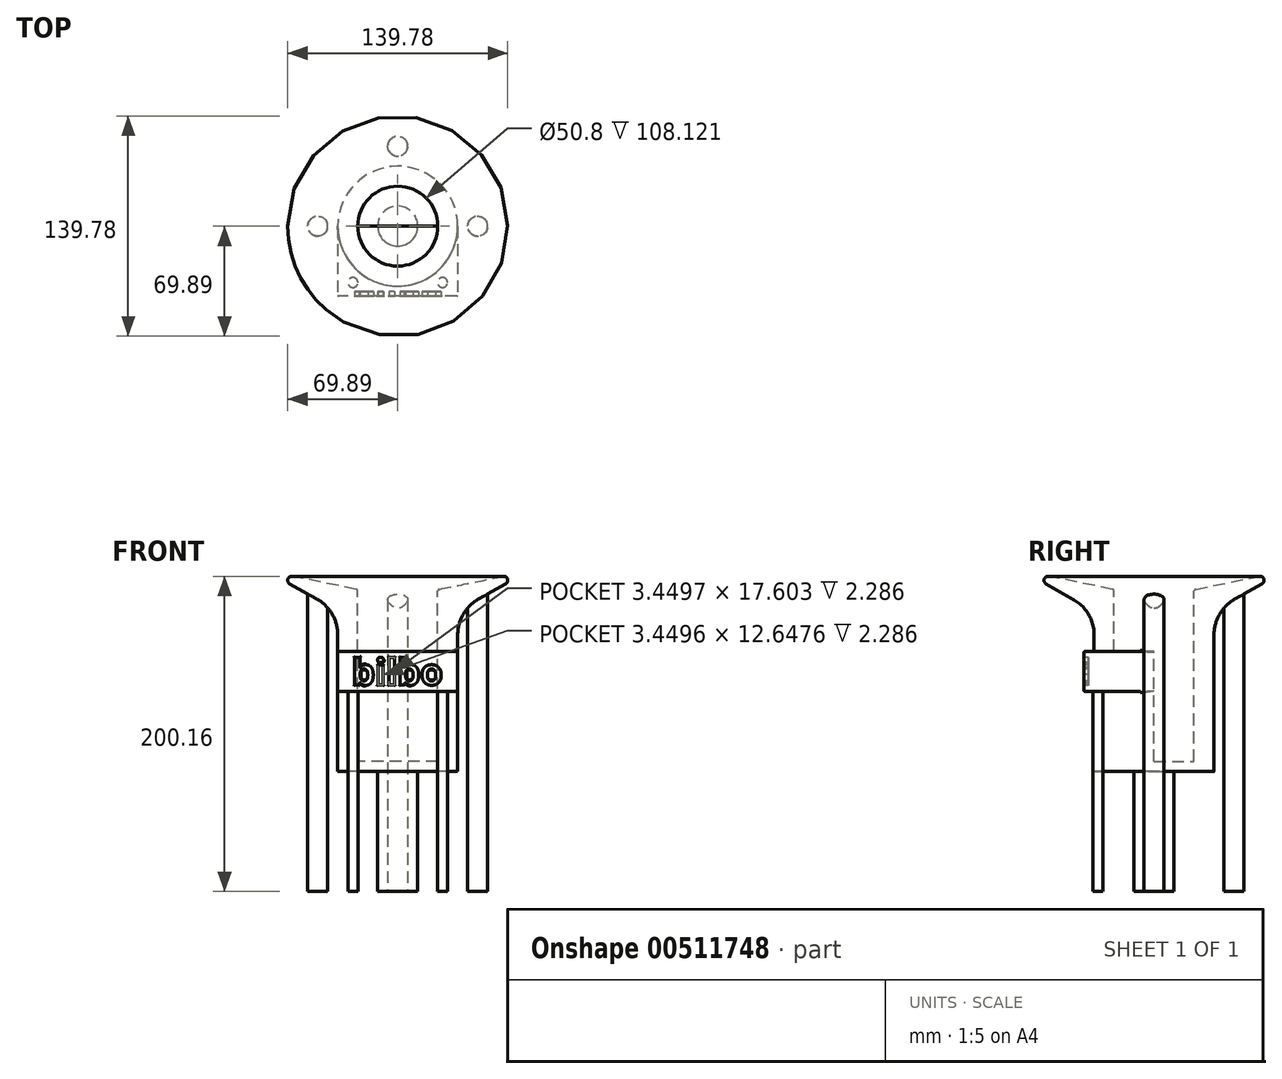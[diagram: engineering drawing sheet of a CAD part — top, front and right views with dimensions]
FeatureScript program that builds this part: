
annotation { "Feature Type Name" : "Feature", "Feature Type Description" : "" }
export const myFeature = defineFeature(function(context is Context, id is Id, definition is map)
    precondition{}
    {
        {
            var Q0;
            Q0=qCreatedBy(makeId("Front.planeOp"),FACE);
            var sketch = newSketch(context, id + "F0", { "sketchPlane" : qUnion([Q0])});
            skLineSegment(sketch, "E0", {"start": v(0, 0) * mm, "end": v(0, -6.35) * mm});
            skLineSegment(sketch, "E1", {"start": v(0, -6.35) * mm, "end": v(38.1, -6.35) * mm});
            skLineSegment(sketch, "E2", {"start": v(38.1, -6.35) * mm, "end": v(38.1, 95.25) * mm});
            skLineSegment(sketch, "E3", {"start": v(38.1, 95.25) * mm, "end": v(82.1, 120.65) * mm});
            skLineSegment(sketch, "E4", {"start": v(0, 0) * mm, "end": v(25.4, 0) * mm});
            skLineSegment(sketch, "E5", {"start": v(25.4, 0) * mm, "end": v(25.4, 109.16) * mm});
            skLineSegment(sketch, "E6", {"start": v(82.1, 120.65) * mm, "end": v(25.4, 109.16) * mm});
            skSolve(sketch);
        }
        {
            var Q0;
            Q0=makeQuery(id+"F0.imprint","IMPRINT",FACE,{"disambiguationData":[TD([[makeQuery(id+"F0.imprint","IMPRINT",EDGE,{"derivedFrom":sQuery(id+"F0.wireOp",EDGE,"E0")}),1.0]])]});
            var Q1;
            Q1=sQuery(id+"F0.wireOp",EDGE,"E0");
            revolve(context, id + "F1", {"entities" : qUnion([Q0]), "axis" : qUnion([Q1]), "revolveType" : RevolveType.FULL});
        }
        {
            var Q0;
            Q0=makeQuery(id+"F1.opRevolve","SWEPT_EDGE",EDGE,{"disambiguationData":[OSD([sQuery(id+"F0.wireOp",EDGE,"E3"),sQuery(id+"F0.wireOp",EDGE,"E6")])]});
            fillet(context, id + "F2", {"entities" : qUnion([Q0]), "radius" : 2.54 * mm, "tangentPropagation" : true, "allowEdgeOverflow" : false});
        }
        {
            var Q0;
            Q0=makeQuery(id+"F1.opRevolve","SWEPT_EDGE",EDGE,{"disambiguationData":[OSD([sQuery(id+"F0.wireOp",EDGE,"E5"),sQuery(id+"F0.wireOp",EDGE,"E6")])]});
            fillet(context, id + "F3", {"entities" : qUnion([Q0]), "radius" : 1.27 * mm, "tangentPropagation" : true, "allowEdgeOverflow" : false});
        }
        {
            var Q0;
            Q0=makeQuery(id+"F1.opRevolve","SWEPT_EDGE",EDGE,{"disambiguationData":[OSD([sQuery(id+"F0.wireOp",EDGE,"E2"),sQuery(id+"F0.wireOp",EDGE,"E3")])]});
            fillet(context, id + "F4", {"entities" : qUnion([Q0]), "radius" : 25.4 * mm, "tangentPropagation" : true, "allowEdgeOverflow" : false});
        }
        {
            var Q0;
            Q0=makeQuery(id+"F1.opRevolve","SWEPT_EDGE",EDGE,{"disambiguationData":[OSD([sQuery(id+"F0.wireOp",EDGE,"E1"),sQuery(id+"F0.wireOp",EDGE,"E2")])]});
            fillet(context, id + "F5", {"entities" : qUnion([Q0]), "radius" : 0.13 * mm, "tangentPropagation" : true, "allowEdgeOverflow" : false});
        }
        {
            var Q0;
            Q0=makeQuery(id+"F1.opRevolve","SWEPT_FACE",FACE,{"disambiguationData":[OSD([sQuery(id+"F0.wireOp",EDGE,"E1")])]});
            var sketch = newSketch(context, id + "F6", { "sketchPlane" : qUnion([Q0])});
            skLineSegment(sketch, "E7", {"start": v(0, 0) * mm, "end": v(-38.1, 0) * mm});
            skLineSegment(sketch, "E8", {"start": v(-38.1, 0) * mm, "end": v(38.1, 0) * mm});
            skLineSegment(sketch, "E9", {"start": v(0, 44.45) * mm, "end": v(-38.1, 44.45) * mm});
            skLineSegment(sketch, "E10", {"start": v(-38.1, 44.45) * mm, "end": v(38.1, 44.45) * mm});
            skLineSegment(sketch, "E11", {"start": v(38.1, 44.45) * mm, "end": v(38.1, 0) * mm});
            skLineSegment(sketch, "E12", {"start": v(-38.1, 44.45) * mm, "end": v(-38.1, 0) * mm});
            skSolve(sketch);
        }
        {
            var Q0;
            Q0 = qSketchRegion(id + "F6", true);
            extrude(context, id + "F7", {"entities" : qUnion([Q0]), "operationType" : NewBodyOperationType.ADD, "depth" : -76.2 * mm});
        }
        {
            var Q0;
            Q0=makeQuery(id+"F7.boolean.opBoolean","MERGE",FACE,{"derivedFrom":[makeQuery(id+"F1.opRevolve","SWEPT_FACE",FACE,{"disambiguationData":[OSD([sQuery(id+"F0.wireOp",EDGE,"E1")])]}),makeQuery(id+"F7.opExtrude","CAP_FACE",FACE,{"disambiguationData":[OSD([sQuery(id+"F6.wireOp",EDGE,"E8"),sQuery(id+"F6.wireOp",EDGE,"E10"),sQuery(id+"F6.wireOp",EDGE,"E11"),sQuery(id+"F6.wireOp",EDGE,"E12")])],"isStart":true})]});
            var sketch = newSketch(context, id + "F8", { "sketchPlane" : qUnion([Q0])});
            skCircle(sketch, "E13", {"center": v(0, 0) * mm, "radius": 38.1 * mm});
            skCircle(sketch, "E14", {"center": v(0, 0) * mm, "radius": 62.93 * mm});
            skSolve(sketch);
        }
        {
            var Q0;
            Q0=makeQuery(id+"F8.imprint","IMPRINT",FACE,{"disambiguationData":[TD([[makeQuery(id+"F8.imprint","IMPRINT",EDGE,{"derivedFrom":sQuery(id+"F8.wireOp",EDGE,"E14")}),1.0]])]});
            var Q1;
            {var subQ3=sQuery(id+"F6.wireOp",EDGE,"E10");Q1=makeQuery(id+"F8.imprint","IMPRINT",FACE,{"disambiguationData":[TD([[makeQuery(id+"F8.imprint","IMPRINT",EDGE,{"derivedFrom":makeQuery(id+"F7.opExtrude","CAP_EDGE",EDGE,{"disambiguationData":[OSD([subQ3])],"isStart":true})}),-1.0]])]});}
            extrude(context, id + "F9", {"entities" : qUnion([Q0, Q1]), "operationType" : NewBodyOperationType.REMOVE, "oppositeDirection" : true, "depth" : 50.8 * mm});
        }
        {
            var Q0;
            Q0=makeQuery(id+"F7.opExtrude","SWEPT_FACE",FACE,{"disambiguationData":[OSD([sQuery(id+"F6.wireOp",EDGE,"E10")])]});
            var sketch = newSketch(context, id + "F10", { "sketchPlane" : qUnion([Q0])});
            skText(sketch, "E15", { "text": "bilbo\n", "fontName": "OpenSans-Bold.ttf"});
            skLineSegment(sketch, "E16.left", {"start": v(63.5, 69.85) * mm, "end": v(63.5, 44.45) * mm});
            skPoint(sketch, "E16.middle", {"position": v(0, 57.15) * mm});
            const initialGuessF10  = {"E15": [-0.0291, 0.04858, 1, 0, 0.01668]};
            skSetInitialGuess(sketch, initialGuessF10);
            skSolve(sketch);
        }
        {
            var Q0;
            Q0 = qSketchRegion(id + "F10", true);
            extrude(context, id + "F11", {"entities" : qUnion([Q0]), "operationType" : NewBodyOperationType.REMOVE, "oppositeDirection" : true, "depth" : 2.8 * mm});
        }
        {
            var Q0;
            {var subQ1=sQuery(id+"F6.wireOp",EDGE,"E11");var subQ2=sQuery(id+"F6.wireOp",EDGE,"E10");Q0=makeQuery(id+"F11.boolean.opBoolean","SPLIT",FACE,{"disambiguationData":[TD([makeQuery(id+"F7.opExtrude","SWEPT_FACE",FACE,{"disambiguationData":[OSD([subQ1])]})])],"derivedFrom":makeQuery(id+"F7.opExtrude","SWEPT_FACE",FACE,{"disambiguationData":[OSD([subQ2])]})});}
            var Q1;
            Q1=makeQuery(id+"F11.boolean.opBoolean","SPLIT",FACE,{"disambiguationData":[TD([makeQuery(id+"F11.opExtrude","SWEPT_FACE",FACE,{"disambiguationData":[OSD([sQuery(id+"F10.wireOp",EDGE,"E15.sketch_text.stroke-14")])]})])],"derivedFrom":makeQuery(id+"F7.opExtrude","SWEPT_FACE",FACE,{"disambiguationData":[OSD([sQuery(id+"F6.wireOp",EDGE,"E10")])]})});
            var Q2;
            Q2=makeQuery(id+"F11.boolean.opBoolean","SPLIT",FACE,{"disambiguationData":[TD([makeQuery(id+"F11.opExtrude","SWEPT_FACE",FACE,{"disambiguationData":[OSD([sQuery(id+"F10.wireOp",EDGE,"E15.sketch_text.stroke-50")])]})])],"derivedFrom":makeQuery(id+"F7.opExtrude","SWEPT_FACE",FACE,{"disambiguationData":[OSD([sQuery(id+"F6.wireOp",EDGE,"E10")])]})});
            var Q3;
            Q3=makeQuery(id+"F11.boolean.opBoolean","SPLIT",FACE,{"disambiguationData":[TD([makeQuery(id+"F11.opExtrude","SWEPT_FACE",FACE,{"disambiguationData":[OSD([sQuery(id+"F10.wireOp",EDGE,"E15.sketch_text.stroke-59")])]})])],"derivedFrom":makeQuery(id+"F7.opExtrude","SWEPT_FACE",FACE,{"disambiguationData":[OSD([sQuery(id+"F6.wireOp",EDGE,"E10")])]})});
            fillet(context, id + "F12", {"entities" : qUnion([Q0, Q1, Q2, Q3]), "radius" : 0.5 * mm, "tangentPropagation" : true, "allowEdgeOverflow" : false});
        }
        {
            var Q0;
            Q0=makeQuery(id+"F7.opExtrude","SWEPT_FACE",FACE,{"disambiguationData":[OSD([sQuery(id+"F6.wireOp",EDGE,"E11")])]});
            var Q1;
            Q1=makeQuery(id+"F9.boolean.opBoolean","COPY",EDGE,{"derivedFrom":makeQuery(id+"F9.opExtrude","CAP_EDGE",EDGE,{"disambiguationData":[OSD([sQuery(id+"F8.wireOp",EDGE,"E13")])],"isStart":false})});
            var Q2;
            Q2=makeQuery(id+"F7.boolean.opBoolean","INTERSECT",EDGE,{"derivedFrom":[makeQuery(id+"F1.opRevolve","SWEPT_FACE",FACE,{"disambiguationData":[OSD([sQuery(id+"F0.wireOp",EDGE,"E2")])]}),makeQuery(id+"F7.opExtrude","CAP_FACE",FACE,{"disambiguationData":[OSD([sQuery(id+"F6.wireOp",EDGE,"E8"),sQuery(id+"F6.wireOp",EDGE,"E10"),sQuery(id+"F6.wireOp",EDGE,"E11"),sQuery(id+"F6.wireOp",EDGE,"E12")])],"isStart":false})]});
            var Q3;
            Q3=makeQuery(id+"F7.opExtrude","SWEPT_FACE",FACE,{"disambiguationData":[OSD([sQuery(id+"F6.wireOp",EDGE,"E12")])]});
            fillet(context, id + "F13", {"entities" : qUnion([Q0, Q1, Q2, Q3]), "radius" : 0.5 * mm, "tangentPropagation" : true, "allowEdgeOverflow" : false});
        }
        {
            var Q0;
            Q0=makeQuery(id+"F7.boolean.opBoolean","MERGE",FACE,{"derivedFrom":[makeQuery(id+"F1.opRevolve","SWEPT_FACE",FACE,{"disambiguationData":[OSD([sQuery(id+"F0.wireOp",EDGE,"E1")])]}),makeQuery(id+"F7.opExtrude","CAP_FACE",FACE,{"disambiguationData":[OSD([sQuery(id+"F6.wireOp",EDGE,"E8"),sQuery(id+"F6.wireOp",EDGE,"E10"),sQuery(id+"F6.wireOp",EDGE,"E11"),sQuery(id+"F6.wireOp",EDGE,"E12")])],"isStart":true})]});
            var sketch = newSketch(context, id + "F14", { "sketchPlane" : qUnion([Q0])});
            skCircle(sketch, "E17", {"center": v(0, 0) * mm, "radius": 12.7 * mm});
            skSolve(sketch);
        }
        {
            var Q0;
            Q0 = qSketchRegion(id + "F14", true);
            extrude(context, id + "F15", {"entities" : qUnion([Q0]), "operationType" : NewBodyOperationType.ADD, "depth" : 76.2 * mm});
        }
        {
            var Q0;
            Q0=makeQuery(id+"F15.opExtrude","CAP_FACE",FACE,{"disambiguationData":[OSD([sQuery(id+"F14.wireOp",EDGE,"E17")])],"isStart":false});
            var sketch = newSketch(context, id + "F16", { "sketchPlane" : qUnion([Q0])});
            skPoint(sketch, "E18.middle", {"position": v(0, 0) * mm});
            skCircle(sketch, "E19", {"center": v(-50.8, 0) * mm, "radius": 6.35 * mm});
            skCircle(sketch, "E20", {"center": v(0, -50.8) * mm, "radius": 6.35 * mm});
            skCircle(sketch, "E21", {"center": v(50.8, 0) * mm, "radius": 6.35 * mm});
            skSolve(sketch);
        }
        {
            var Q0;
            Q0 = qSketchRegion(id + "F16", true);
            extrude(context, id + "F17", {"entities" : qUnion([Q0]), "operationType" : NewBodyOperationType.ADD, "endBound" : BoundingType.UP_TO_NEXT, "oppositeDirection" : true, "depth" : 25.4 * mm});
        }
        {
            var Q0;
            Q0=makeQuery(id+"F15.opExtrude","CAP_FACE",FACE,{"disambiguationData":[OSD([sQuery(id+"F14.wireOp",EDGE,"E17")])],"isStart":false});
            var sketch = newSketch(context, id + "F18", { "sketchPlane" : qUnion([Q0])});
            skLineSegment(sketch, "E22", {"start": v(0, 0) * mm, "end": v(-28.46, 35.78) * mm, "construction": true});
            skCircle(sketch, "E23", {"center": v(-28.46, 35.78) * mm, "radius": 3.18 * mm});
            skLineSegment(sketch, "E24", {"start": v(0, 0) * mm, "end": v(0, 59.1) * mm, "construction": true});
            skLineSegment(sketch, "E25", {"start": v(0, 0) * mm, "end": v(28.46, 35.78) * mm, "construction": true});
            skCircle(sketch, "E26", {"center": v(28.46, 35.78) * mm, "radius": 3.18 * mm});
            skSolve(sketch);
        }
        {
            var Q0;
            Q0 = qSketchRegion(id + "F18", true);
            extrude(context, id + "F19", {"entities" : qUnion([Q0]), "operationType" : NewBodyOperationType.ADD, "endBound" : BoundingType.UP_TO_NEXT, "oppositeDirection" : true, "depth" : 25.4 * mm});
        }
    });
